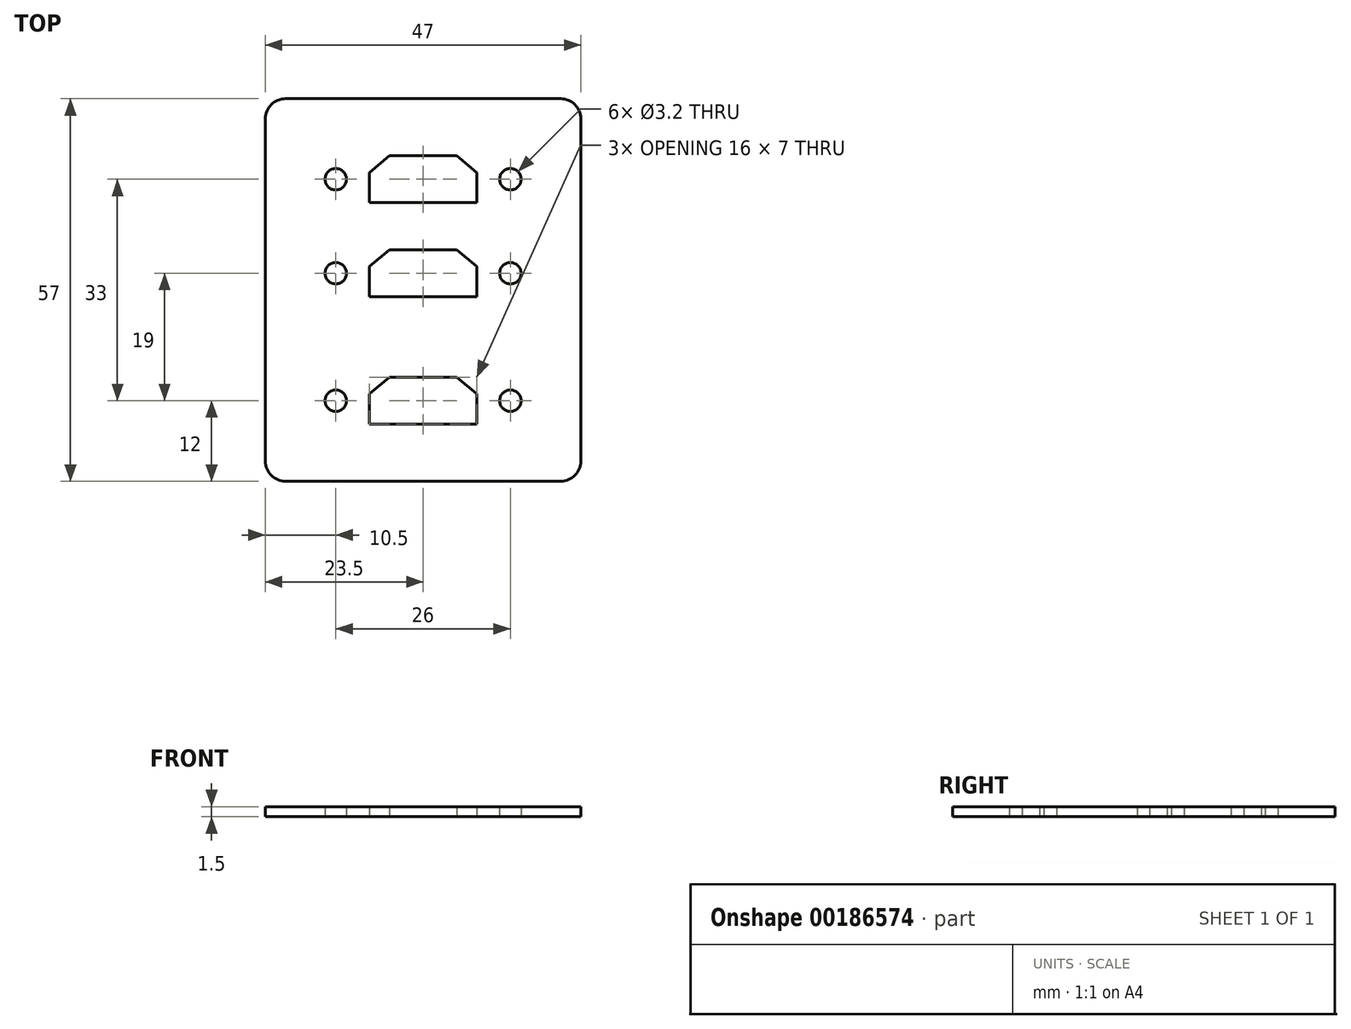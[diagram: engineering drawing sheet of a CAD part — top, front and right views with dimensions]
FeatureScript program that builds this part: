
annotation { "Feature Type Name" : "Feature", "Feature Type Description" : "" }
export const myFeature = defineFeature(function(context is Context, id is Id, definition is map)
    precondition{}
    {
        {
            var Q0;
            Q0=qCreatedBy(makeId("Top.planeOp"),FACE);
            var sketch = newSketch(context, id + "F0", { "sketchPlane" : qUnion([Q0])});
            skCircle(sketch, "E0", {"center": v(13, 0) * mm, "radius": 1.6 * mm});
            skCircle(sketch, "E1.MirrorC", {"center": v(-13, 0) * mm, "radius": 1.6 * mm});
            skLineSegment(sketch, "E2", {"start": v(-67.52, 7) * mm, "end": v(-61.9, 7) * mm});
            skLineSegment(sketch, "E3", {"start": v(-68.04, -7) * mm, "end": v(-60.74, -7) * mm});
            skCircle(sketch, "E4.MirrorC", {"center": v(13, 14) * mm, "radius": 1.6 * mm});
            skCircle(sketch, "E5.MirrorC", {"center": v(-13, 14) * mm, "radius": 1.6 * mm});
            skLineSegment(sketch, "E6.bottom", {"start": v(20.5, -31) * mm, "end": v(-20.5, -31) * mm});
            skLineSegment(sketch, "E6.top", {"start": v(20.5, 26) * mm, "end": v(-20.5, 26) * mm});
            skLineSegment(sketch, "E6.left", {"start": v(23.5, -28) * mm, "end": v(23.5, 23) * mm});
            skLineSegment(sketch, "E6.right", {"start": v(-23.5, -28) * mm, "end": v(-23.5, 23) * mm});
            skPoint(sketch, "E7.visualSharp", {"position": v(-23.5, 26) * mm});
            skArc(sketch, "E7.filletArc", {"start": v(-20.5, 26) * mm, "mid": v(-22.62, 25.12) * mm, "end": v(-23.5, 23) * mm});
            skPoint(sketch, "E8.visualSharp", {"position": v(23.5, 26) * mm});
            skArc(sketch, "E8.filletArc", {"start": v(23.5, 23) * mm, "mid": v(22.62, 25.12) * mm, "end": v(20.5, 26) * mm});
            skPoint(sketch, "E9.visualSharp", {"position": v(23.5, -31) * mm});
            skArc(sketch, "E9.filletArc", {"start": v(20.5, -31) * mm, "mid": v(22.62, -30.12) * mm, "end": v(23.5, -28) * mm});
            skPoint(sketch, "E10.visualSharp", {"position": v(-23.5, -31) * mm});
            skArc(sketch, "E10.filletArc", {"start": v(-23.5, -28) * mm, "mid": v(-22.62, -30.12) * mm, "end": v(-20.5, -31) * mm});
            skPoint(sketch, "E11.MirrorP", {"position": v(23.5, -26) * mm});
            skPoint(sketch, "E12.MirrorP", {"position": v(-23.5, -26) * mm});
            skLineSegment(sketch, "E13", {"start": v(-5, 3.5) * mm, "end": v(5, 3.5) * mm});
            skLineSegment(sketch, "E14", {"start": v(-8, -3.5) * mm, "end": v(8, -3.5) * mm});
            skPoint(sketch, "E15", {"position": v(0, -3.5) * mm});
            skPoint(sketch, "E16", {"position": v(0, 3.5) * mm});
            skLineSegment(sketch, "E17", {"start": v(-8, -3.5) * mm, "end": v(-8, 1) * mm});
            skLineSegment(sketch, "E18", {"start": v(-8, 1) * mm, "end": v(-5, 3.5) * mm});
            skLineSegment(sketch, "E19", {"start": v(8, -3.5) * mm, "end": v(8, 1) * mm});
            skLineSegment(sketch, "E20", {"start": v(8, 1) * mm, "end": v(5, 3.5) * mm});
            skLineSegment(sketch, "E21", {"start": v(-5, 17.5) * mm, "end": v(5, 17.5) * mm});
            skLineSegment(sketch, "E22", {"start": v(-8, 10.5) * mm, "end": v(8, 10.5) * mm});
            skPoint(sketch, "E23", {"position": v(0, 10.5) * mm});
            skPoint(sketch, "E24", {"position": v(0, 17.5) * mm});
            skLineSegment(sketch, "E25", {"start": v(-8, 10.5) * mm, "end": v(-8, 15) * mm});
            skLineSegment(sketch, "E26", {"start": v(-8, 15) * mm, "end": v(-5, 17.5) * mm});
            skLineSegment(sketch, "E27", {"start": v(8, 10.5) * mm, "end": v(8, 15) * mm});
            skLineSegment(sketch, "E28", {"start": v(8, 15) * mm, "end": v(5, 17.5) * mm});
            skPoint(sketch, "E29", {"position": v(-8, 14) * mm});
            skLineSegment(sketch, "E30", {"start": v(-5, -15.5) * mm, "end": v(5, -15.5) * mm});
            skLineSegment(sketch, "E31", {"start": v(-8, -22.5) * mm, "end": v(8, -22.5) * mm});
            skPoint(sketch, "E32", {"position": v(0, -22.5) * mm});
            skPoint(sketch, "E33", {"position": v(0, -15.5) * mm});
            skLineSegment(sketch, "E34", {"start": v(-8, -22.5) * mm, "end": v(-8, -18) * mm});
            skLineSegment(sketch, "E35", {"start": v(-8, -18) * mm, "end": v(-5, -15.5) * mm});
            skLineSegment(sketch, "E36", {"start": v(8, -22.5) * mm, "end": v(8, -18) * mm});
            skLineSegment(sketch, "E37", {"start": v(8, -18) * mm, "end": v(5, -15.5) * mm});
            skPoint(sketch, "E38", {"position": v(0, -31) * mm});
            skPoint(sketch, "E39", {"position": v(-23.5, -2.5) * mm});
            skCircle(sketch, "E40", {"center": v(-13, -19) * mm, "radius": 1.6 * mm});
            skCircle(sketch, "E41", {"center": v(13, -19) * mm, "radius": 1.6 * mm});
            skSolve(sketch);
        }
        {
            var Q0;
            Q0=qSketchRegion(id+"F0",true);
            extrude(context, id + "F1", {"entities" : qUnion([Q0]), "depth" : 1.5 * mm});
        }
    });
